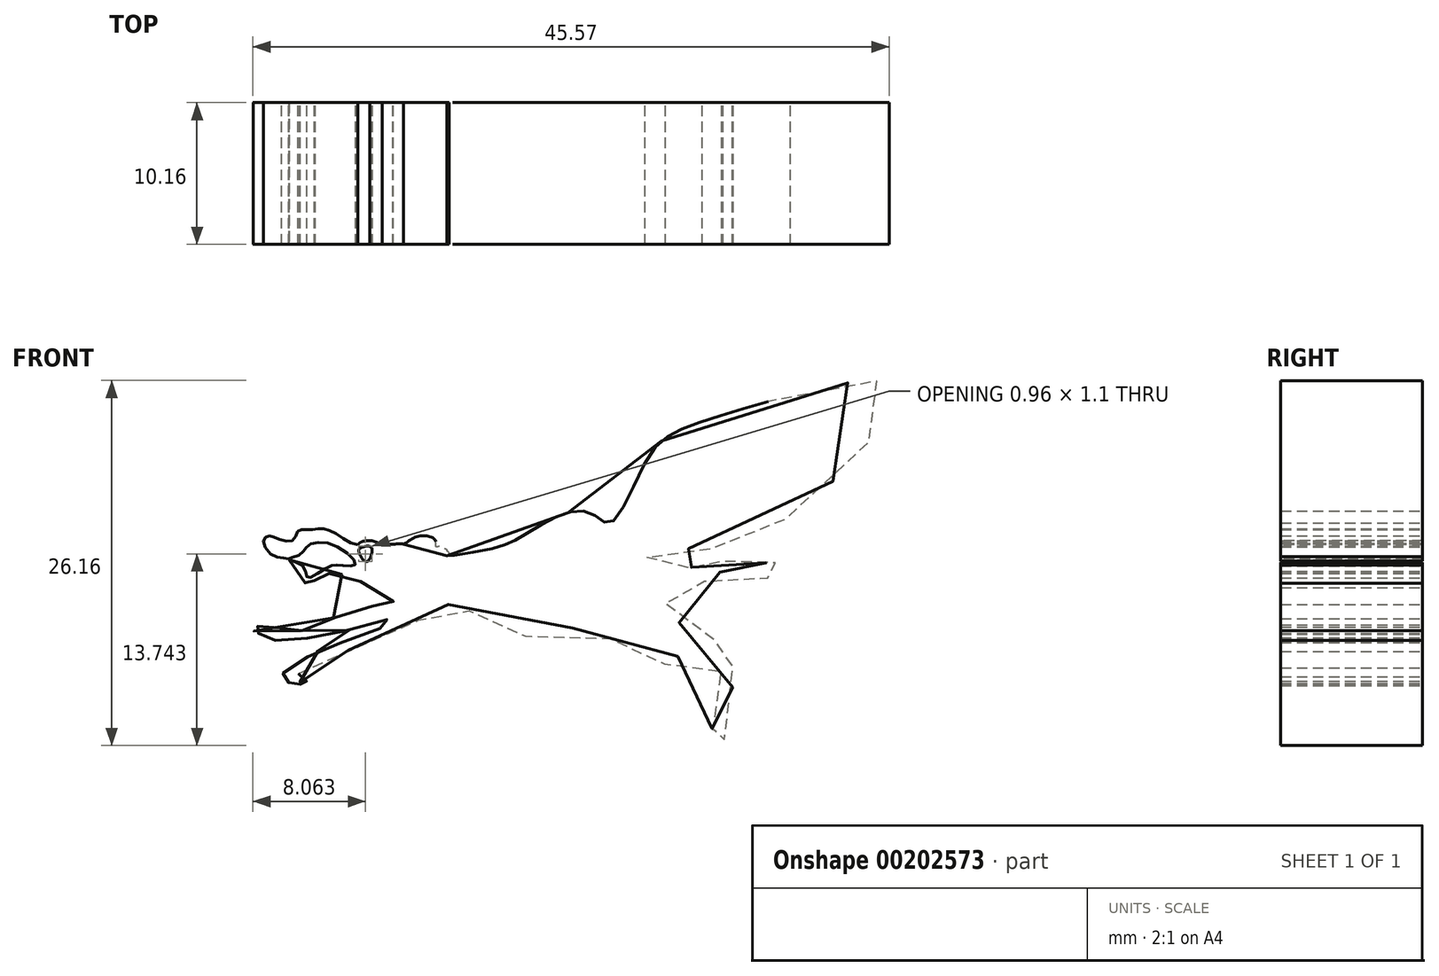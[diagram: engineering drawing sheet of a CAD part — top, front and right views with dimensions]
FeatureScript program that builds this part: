
annotation { "Feature Type Name" : "Feature", "Feature Type Description" : "" }
export const myFeature = defineFeature(function(context is Context, id is Id, definition is map)
    precondition{}
    {
        {
            var Q0;
            Q0=qCreatedBy(makeId("Front.planeOp"),FACE);
            var sketch = newSketch(context, id + "F0", { "sketchPlane" : qUnion([Q0])});
            skFitSpline(sketch, "E0", {"points": [v(-5.68, -3.1) * mm, v(-6.34, -3.17) * mm, v(-6.7, -3.83) * mm, v(-7.81, -3.72) * mm, v(-8.44, -3.54) * mm, v(-8.84, -3.87) * mm, v(-8.03, -5.01) * mm, v(-7.04, -5.2) * mm, v(-6.41, -6.37) * mm, v(-5.12, -7.22) * mm, v(-5.2, -6.78) * mm, v(-4.68, -6.6) * mm, v(-4.2, -6.26) * mm, v(-2.5, -6.52) * mm, v(0.48, -8.25) * mm, v(0, -8.36) * mm, v(-2.25, -8.92) * mm, v(-5.42, -10.02) * mm, v(-6.93, -10.5) * mm, v(-8, -9.95) * mm, v(-9.14, -9.99) * mm, v(-9.58, -10.13) * mm, v(-9.32, -10.58) * mm, v(-8.96, -10.32) * mm, v(-7.92, -11.05) * mm, v(-5.6, -10.83) * mm, v(-2.36, -10.2) * mm, v(0.44, -9.47) * mm, v(-1.22, -10.5) * mm, v(-4.64, -11.64) * mm, v(-6.6, -12.79) * mm, v(-7.55, -13.7) * mm, v(-7.11, -14.22) * mm, v(-7, -13.95) * mm, v(-6.72, -14.21) * mm, v(-6.19, -14.15) * mm, v(-6.32, -13.93) * mm, v(-5.86, -14.1) * mm, v(-5.8, -13.7) * mm, v(-6.3, -13.62) * mm, v(-6.28, -13.3) * mm, v(-4.53, -12.33) * mm, v(-1.36, -11.2) * mm, v(1.35, -9.92) * mm, v(2.4, -9.5) * mm, v(3.67, -8.62) * mm, v(5.6, -8.72) * mm, v(7.77, -10.5) * mm, v(9.48, -10.79) * mm, v(15.07, -10.15) * mm, v(16.5, -11.62) * mm, v(18.91, -13) * mm, v(20.88, -12.16) * mm, v(23.51, -12.2) * mm, v(24, -15.64) * mm, v(23.96, -17.07) * mm, v(22.86, -17.6) * mm, v(22.68, -18.51) * mm, v(23.44, -18.36) * mm, v(24.54, -17.88) * mm, v(24.76, -15.63) * mm, v(24.66, -10.62) * mm, v(24.36, -10.32) * mm, v(23.71, -10.84) * mm, v(22.33, -10.8) * mm, v(20.03, -8.64) * mm, v(20.1, -8.09) * mm, v(21.43, -7.06) * mm, v(22.63, -6.86) * mm, v(23.31, -6.31) * mm, v(26.52, -6.29) * mm, v(28.52, -6.94) * mm, v(28.92, -6.66) * mm, v(27.9, -5.48) * mm, v(26.37, -5.63) * mm, v(24.74, -5.36) * mm, v(23.18, -5.3) * mm, v(22.6, -5) * mm, v(22.06, -5.38) * mm, v(21.6, -5.96) * mm, v(19, -6.03) * mm, v(18.77, -5.3) * mm, v(18.5, -4.84) * mm, v(20.74, -4.47) * mm, v(25.69, -4.13) * mm, v(28.57, -2.33) * mm, v(34, 2.47) * mm, v(35.98, 6.77) * mm, v(35.32, 7.53) * mm, v(29.5, 6.68) * mm, v(21.88, 4.4) * mm, v(18.81, 2.23) * mm, v(16.02, -2.6) * mm, v(14.65, -1.93) * mm, v(12.38, -2.07) * mm, v(9.4, -3.73) * mm, v(7.38, -4.47) * mm, v(4.3, -4.96) * mm, v(4.46, -4.81) * mm, v(3.83, -4.3) * mm, v(3.54, -4.3) * mm, v(3.48, -3.88) * mm, v(2.98, -3.56) * mm, v(2.05, -3.62) * mm, v(1.2, -4.12) * mm, v(0.64, -4.12) * mm, v(-0.43, -4.09) * mm, v(-1.2, -3.88) * mm, v(-2.07, -4.18) * mm, v(-3.74, -3.31) * mm, v(-4.78, -3.02) * mm, v(-5.68, -3.1) * mm]});
            skFitSpline(sketch, "E1", {"points": [v(-7.04, -5.2) * mm, v(-6.21, -4.86) * mm, v(-5.68, -4.27) * mm, v(-3.92, -4.15) * mm, v(-2.25, -5.58) * mm, v(-3.35, -5.64) * mm, v(-4.2, -5.76) * mm, v(-5.68, -6.52) * mm, v(-5.98, -5.73) * mm, v(-7.04, -5.2) * mm]});
            skFitSpline(sketch, "E2", {"points": [v(1.2, -4.12) * mm, v(2.07, -4.73) * mm, v(2.07, -5.53) * mm, v(1.2, -6.16) * mm, v(-0.43, -6.06) * mm, v(-1.5, -5.37) * mm, v(-2.07, -4.18) * mm, v(-1.2, -3.88) * mm, v(-0.43, -4.09) * mm, v(0.64, -4.12) * mm, v(1.2, -4.12) * mm]});
            skFitSpline(sketch, "E3", {"points": [v(-2, -4.65) * mm, v(-1.81, -4.36) * mm, v(-1.15, -4.33) * mm, v(-1.12, -4.97) * mm, v(-1.5, -5.37) * mm, v(-2, -4.65) * mm]});
            skSolve(sketch);
        }
        {
            var Q0;
            {var subQ0=sQuery(id+"F0.wireOp",EDGE,"E1");var subQ1=sQuery(id+"F0.wireOp",EDGE,"E0");var subQ2=makeQuery(id+"F0.imprint","INTERSECT",VERTEX,{"disambiguationData":[OD(0.0)],"derivedFrom":[subQ1,subQ0]});Q0=makeQuery(id+"F0.imprint","IMPRINT",FACE,{"disambiguationData":[TD([[makeQuery(id+"F0.imprint","IMPRINT",EDGE,{"disambiguationData":[TD([[subQ2,1.0]])],"derivedFrom":subQ1}),-1.0]])]});}
            var Q1;
            {var subQ0=sQuery(id+"F0.wireOp",EDGE,"E2");var subQ1=sQuery(id+"F0.wireOp",EDGE,"E0");var subQ2=makeQuery(id+"F0.imprint","INTERSECT",VERTEX,{"disambiguationData":[OD(0.0)],"derivedFrom":[subQ1,subQ0]});Q1=makeQuery(id+"F0.imprint","IMPRINT",FACE,{"disambiguationData":[TD([[makeQuery(id+"F0.imprint","IMPRINT",EDGE,{"disambiguationData":[TD([[subQ2,-1.0]])],"derivedFrom":subQ1}),-1.0]])]});}
            var Q2;
            {var subQ0=sQuery(id+"F0.wireOp",EDGE,"E2");var subQ1=sQuery(id+"F0.wireOp",EDGE,"E0");var subQ2=makeQuery(id+"F0.imprint","INTERSECT",VERTEX,{"disambiguationData":[OD(3.0)],"derivedFrom":[subQ1,subQ0]});Q2=makeQuery(id+"F0.imprint","IMPRINT",FACE,{"disambiguationData":[TD([[makeQuery(id+"F0.imprint","IMPRINT",EDGE,{"disambiguationData":[TD([[subQ2,-1.0]])],"derivedFrom":subQ1}),1.0]])]});}
            var Q3;
            {var subQ0=sQuery(id+"F0.wireOp",EDGE,"E2");var subQ1=sQuery(id+"F0.wireOp",EDGE,"E0");var subQ2=makeQuery(id+"F0.imprint","INTERSECT",VERTEX,{"disambiguationData":[OD(4.0)],"derivedFrom":[subQ1,subQ0]});Q3=makeQuery(id+"F0.imprint","IMPRINT",FACE,{"disambiguationData":[TD([[makeQuery(id+"F0.imprint","IMPRINT",EDGE,{"disambiguationData":[TD([[subQ2,-1.0]])],"derivedFrom":subQ1}),-1.0]])]});}
            var Q4;
            {var subQ0=sQuery(id+"F0.wireOp",EDGE,"E2");var subQ1=sQuery(id+"F0.wireOp",EDGE,"E0");var subQ2=makeQuery(id+"F0.imprint","INTERSECT",VERTEX,{"disambiguationData":[OD(1.0)],"derivedFrom":[subQ1,subQ0]});Q4=makeQuery(id+"F0.imprint","IMPRINT",FACE,{"disambiguationData":[TD([[makeQuery(id+"F0.imprint","IMPRINT",EDGE,{"disambiguationData":[TD([[subQ2,1.0]])],"derivedFrom":subQ1}),1.0]])]});}
            var Q5;
            {var subQ0=sQuery(id+"F0.wireOp",EDGE,"E2");var subQ1=sQuery(id+"F0.wireOp",EDGE,"E0");var subQ2=makeQuery(id+"F0.imprint","INTERSECT",VERTEX,{"disambiguationData":[OD(0.0)],"derivedFrom":[subQ1,subQ0]});Q5=makeQuery(id+"F0.imprint","IMPRINT",FACE,{"disambiguationData":[TD([[makeQuery(id+"F0.imprint","IMPRINT",EDGE,{"disambiguationData":[TD([[subQ2,1.0]])],"derivedFrom":subQ1}),1.0]])]});}
            var Q6;
            {var subQ0=sQuery(id+"F0.wireOp",EDGE,"E2");var subQ1=sQuery(id+"F0.wireOp",EDGE,"E0");var subQ2=makeQuery(id+"F0.imprint","INTERSECT",VERTEX,{"disambiguationData":[OD(0.0)],"derivedFrom":[subQ1,subQ0]});Q6=makeQuery(id+"F0.imprint","IMPRINT",FACE,{"disambiguationData":[TD([[makeQuery(id+"F0.imprint","IMPRINT",EDGE,{"disambiguationData":[TD([[subQ2,-1.0]])],"derivedFrom":subQ1}),1.0]])]});}
            extrude(context, id + "F1", {"entities" : qUnion([Q0, Q1, Q2, Q3, Q4, Q5, Q6]), "oppositeDirection" : true, "depth" : 10.16 * mm});
        }
    });
